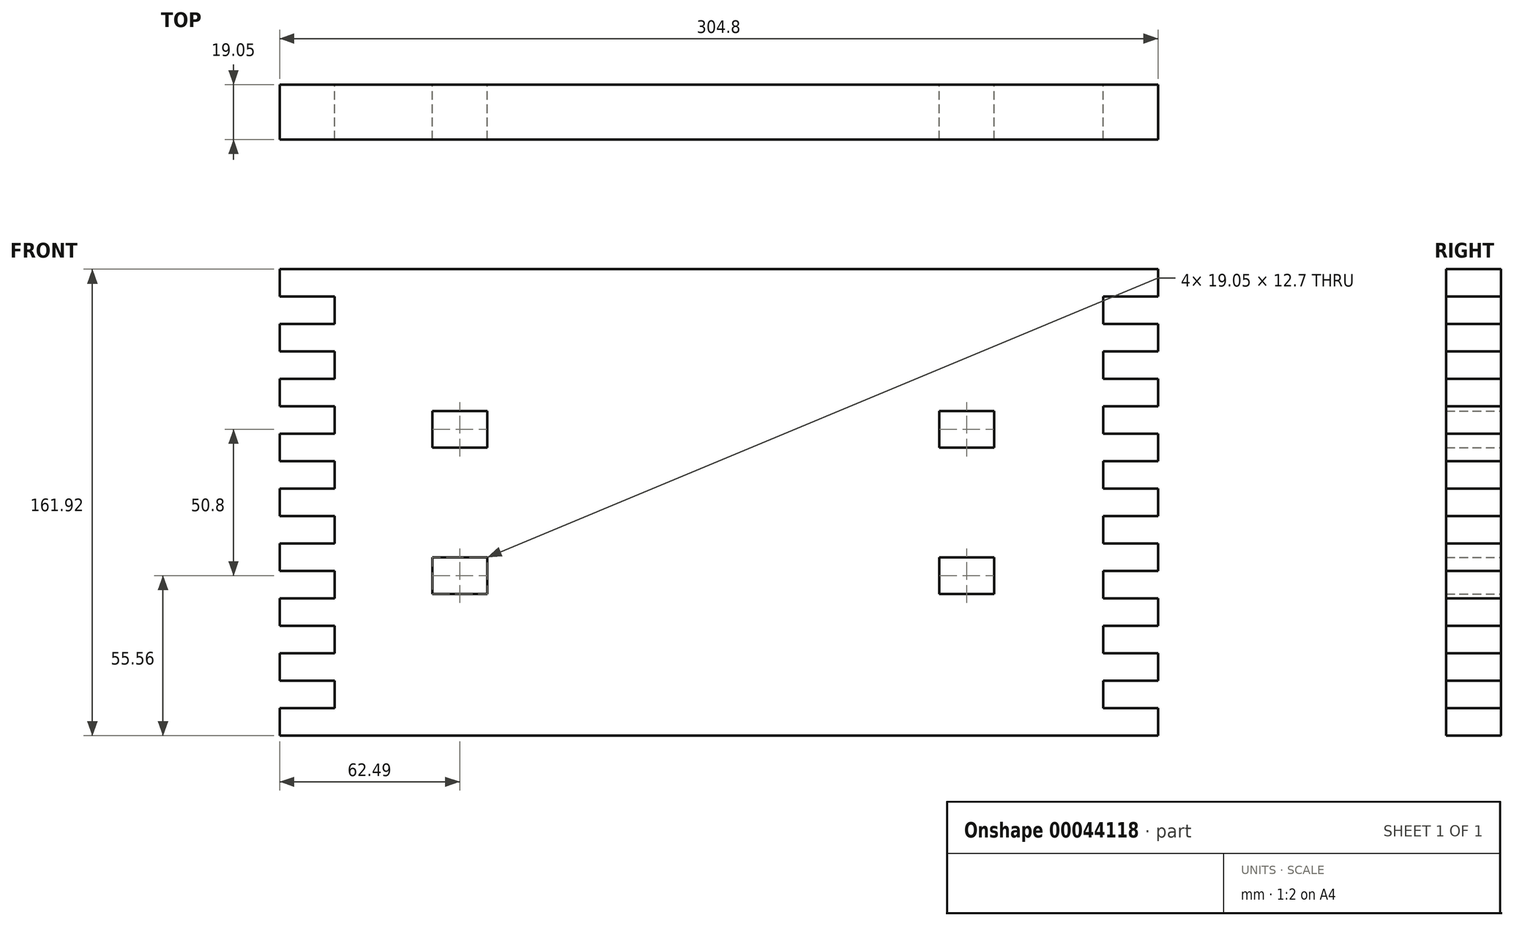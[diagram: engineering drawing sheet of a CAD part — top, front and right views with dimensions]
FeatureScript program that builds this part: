
annotation { "Feature Type Name" : "Feature", "Feature Type Description" : "" }
export const myFeature = defineFeature(function(context is Context, id is Id, definition is map)
    precondition{}
    {
        {
            var Q0;
            Q0=qCreatedBy(makeId("Front.planeOp"),FACE);
            var sketch = newSketch(context, id + "F0", { "sketchPlane" : qUnion([Q0])});
            skPoint(sketch, "E0.rect.middle", {"position": v(0, 0) * mm});
            skLineSegment(sketch, "E1.bottom", {"start": v(-99.44, 19.05) * mm, "end": v(-80.39, 19.05) * mm});
            skLineSegment(sketch, "E1.top", {"start": v(-99.44, 31.75) * mm, "end": v(-80.39, 31.75) * mm});
            skLineSegment(sketch, "E1.left", {"start": v(-99.44, 19.05) * mm, "end": v(-99.44, 31.75) * mm});
            skLineSegment(sketch, "E1.right", {"start": v(-80.39, 19.05) * mm, "end": v(-80.39, 31.75) * mm});
            skLineSegment(sketch, "E2.bottom", {"start": v(-99.44, -19.05) * mm, "end": v(-80.39, -19.05) * mm});
            skLineSegment(sketch, "E2.top", {"start": v(-99.44, -31.75) * mm, "end": v(-80.39, -31.75) * mm});
            skLineSegment(sketch, "E2.left", {"start": v(-99.44, -19.05) * mm, "end": v(-99.44, -31.75) * mm});
            skLineSegment(sketch, "E2.right", {"start": v(-80.39, -19.05) * mm, "end": v(-80.39, -31.75) * mm});
            skLineSegment(sketch, "E3.bottom", {"start": v(76.49, 31.75) * mm, "end": v(95.54, 31.75) * mm});
            skLineSegment(sketch, "E3.top", {"start": v(76.49, 19.05) * mm, "end": v(95.54, 19.05) * mm});
            skLineSegment(sketch, "E3.left", {"start": v(76.49, 31.75) * mm, "end": v(76.49, 19.05) * mm});
            skLineSegment(sketch, "E3.right", {"start": v(95.54, 31.75) * mm, "end": v(95.54, 19.05) * mm});
            skLineSegment(sketch, "E4.bottom", {"start": v(76.49, -19.05) * mm, "end": v(95.54, -19.05) * mm});
            skLineSegment(sketch, "E4.top", {"start": v(76.49, -31.75) * mm, "end": v(95.54, -31.75) * mm});
            skLineSegment(sketch, "E4.left", {"start": v(76.49, -19.05) * mm, "end": v(76.49, -31.75) * mm});
            skLineSegment(sketch, "E4.right", {"start": v(95.54, -19.05) * mm, "end": v(95.54, -31.75) * mm});
            skLineSegment(sketch, "E5", {"start": v(0, -80.96) * mm, "end": v(152.4, -80.96) * mm});
            skLineSegment(sketch, "E6", {"start": v(152.4, 80.96) * mm, "end": v(-152.4, 80.96) * mm});
            skLineSegment(sketch, "E7", {"start": v(133.35, 71.44) * mm, "end": v(133.35, 61.91) * mm});
            skLineSegment(sketch, "E8", {"start": v(133.35, 71.44) * mm, "end": v(152.4, 71.44) * mm});
            skLineSegment(sketch, "E9", {"start": v(152.4, 80.96) * mm, "end": v(152.4, 71.44) * mm});
            skLineSegment(sketch, "E10", {"start": v(133.35, 61.91) * mm, "end": v(152.4, 61.91) * mm});
            skLineSegment(sketch, "E11", {"start": v(152.4, 61.91) * mm, "end": v(152.4, 52.39) * mm});
            skLineSegment(sketch, "E12", {"start": v(152.4, 52.39) * mm, "end": v(133.35, 52.39) * mm});
            skLineSegment(sketch, "E13", {"start": v(133.35, 42.86) * mm, "end": v(152.4, 42.86) * mm});
            skLineSegment(sketch, "E14", {"start": v(152.4, 42.86) * mm, "end": v(152.4, 33.34) * mm});
            skLineSegment(sketch, "E15", {"start": v(152.4, 33.34) * mm, "end": v(133.35, 33.34) * mm});
            skLineSegment(sketch, "E16", {"start": v(133.35, 23.81) * mm, "end": v(152.4, 23.81) * mm});
            skLineSegment(sketch, "E17", {"start": v(152.4, 23.81) * mm, "end": v(152.4, 14.29) * mm});
            skLineSegment(sketch, "E18", {"start": v(152.4, 14.29) * mm, "end": v(133.35, 14.29) * mm});
            skLineSegment(sketch, "E19", {"start": v(133.35, 4.76) * mm, "end": v(152.4, 4.76) * mm});
            skLineSegment(sketch, "E20", {"start": v(152.4, 4.76) * mm, "end": v(152.4, -4.76) * mm});
            skLineSegment(sketch, "E21", {"start": v(152.4, -4.76) * mm, "end": v(133.35, -4.76) * mm});
            skLineSegment(sketch, "E22", {"start": v(133.35, -14.29) * mm, "end": v(152.4, -14.29) * mm});
            skLineSegment(sketch, "E23", {"start": v(152.4, -14.29) * mm, "end": v(152.4, -23.81) * mm});
            skLineSegment(sketch, "E24", {"start": v(152.4, -23.81) * mm, "end": v(133.35, -23.81) * mm});
            skLineSegment(sketch, "E25", {"start": v(133.35, -33.34) * mm, "end": v(152.4, -33.34) * mm});
            skLineSegment(sketch, "E26", {"start": v(152.4, -33.34) * mm, "end": v(152.4, -42.86) * mm});
            skLineSegment(sketch, "E27", {"start": v(152.4, -42.86) * mm, "end": v(133.35, -42.86) * mm});
            skLineSegment(sketch, "E28", {"start": v(133.35, -52.39) * mm, "end": v(152.4, -52.39) * mm});
            skLineSegment(sketch, "E29", {"start": v(152.4, -52.39) * mm, "end": v(152.4, -61.91) * mm});
            skLineSegment(sketch, "E30", {"start": v(152.4, -61.91) * mm, "end": v(133.35, -61.91) * mm});
            skLineSegment(sketch, "E31", {"start": v(152.4, -80.96) * mm, "end": v(152.4, -71.44) * mm});
            skLineSegment(sketch, "E32", {"start": v(152.4, -71.44) * mm, "end": v(133.35, -71.44) * mm});
            skPoint(sketch, "E33.MirrorCS.start.orphan", {"position": v(-152.4, 80.96) * mm});
            skPoint(sketch, "E34.orphan", {"position": v(-152.4, -80.96) * mm});
            skLineSegment(sketch, "E35", {"start": v(0, -80.96) * mm, "end": v(-152.4, -80.96) * mm});
            skLineSegment(sketch, "E36", {"start": v(-152.4, -80.96) * mm, "end": v(-152.4, -71.44) * mm});
            skLineSegment(sketch, "E37", {"start": v(-152.4, -71.44) * mm, "end": v(-133.35, -71.44) * mm});
            skLineSegment(sketch, "E38", {"start": v(-133.35, -71.44) * mm, "end": v(-133.35, -61.91) * mm});
            skLineSegment(sketch, "E39", {"start": v(-133.35, -61.91) * mm, "end": v(-152.4, -61.91) * mm});
            skLineSegment(sketch, "E40", {"start": v(-152.4, -61.91) * mm, "end": v(-152.4, -52.39) * mm});
            skLineSegment(sketch, "E41", {"start": v(-152.4, -52.39) * mm, "end": v(-133.35, -52.39) * mm});
            skLineSegment(sketch, "E42", {"start": v(-133.35, -52.39) * mm, "end": v(-133.35, -42.86) * mm});
            skLineSegment(sketch, "E43", {"start": v(-133.35, -42.86) * mm, "end": v(-152.4, -42.86) * mm});
            skLineSegment(sketch, "E44", {"start": v(-152.4, -42.86) * mm, "end": v(-152.4, -33.34) * mm});
            skLineSegment(sketch, "E45", {"start": v(-152.4, -33.34) * mm, "end": v(-133.35, -33.34) * mm});
            skLineSegment(sketch, "E46", {"start": v(-133.35, -33.34) * mm, "end": v(-133.35, -23.81) * mm});
            skLineSegment(sketch, "E47", {"start": v(-133.35, -23.81) * mm, "end": v(-152.4, -23.81) * mm});
            skLineSegment(sketch, "E48", {"start": v(-152.4, -23.81) * mm, "end": v(-152.4, -14.29) * mm});
            skLineSegment(sketch, "E49", {"start": v(-152.4, -14.29) * mm, "end": v(-133.35, -14.29) * mm});
            skLineSegment(sketch, "E50", {"start": v(-133.35, -14.29) * mm, "end": v(-133.35, -4.76) * mm});
            skLineSegment(sketch, "E51", {"start": v(-133.35, -4.76) * mm, "end": v(-152.4, -4.76) * mm});
            skLineSegment(sketch, "E52", {"start": v(-152.4, -4.76) * mm, "end": v(-152.4, 4.76) * mm});
            skLineSegment(sketch, "E53", {"start": v(-152.4, 4.76) * mm, "end": v(-133.35, 4.76) * mm});
            skLineSegment(sketch, "E54", {"start": v(-133.35, 4.76) * mm, "end": v(-133.35, 14.29) * mm});
            skLineSegment(sketch, "E55", {"start": v(-133.35, 14.29) * mm, "end": v(-152.4, 14.29) * mm});
            skLineSegment(sketch, "E56", {"start": v(-152.4, 14.29) * mm, "end": v(-152.4, 23.81) * mm});
            skLineSegment(sketch, "E57", {"start": v(-152.4, 23.81) * mm, "end": v(-133.35, 23.81) * mm});
            skLineSegment(sketch, "E58", {"start": v(-133.35, 23.81) * mm, "end": v(-133.35, 33.34) * mm});
            skLineSegment(sketch, "E59", {"start": v(-133.35, 33.34) * mm, "end": v(-152.4, 33.34) * mm});
            skLineSegment(sketch, "E60", {"start": v(-152.4, 33.34) * mm, "end": v(-152.4, 42.86) * mm});
            skLineSegment(sketch, "E61", {"start": v(-152.4, 42.86) * mm, "end": v(-133.35, 42.86) * mm});
            skLineSegment(sketch, "E62", {"start": v(-133.35, 42.86) * mm, "end": v(-133.35, 52.39) * mm});
            skLineSegment(sketch, "E63", {"start": v(-133.35, 71.44) * mm, "end": v(-152.4, 71.44) * mm});
            skLineSegment(sketch, "E64", {"start": v(-152.4, 71.44) * mm, "end": v(-152.4, 80.96) * mm});
            skLineSegment(sketch, "E65", {"start": v(-133.35, 52.39) * mm, "end": v(-152.4, 52.39) * mm});
            skLineSegment(sketch, "E66", {"start": v(-152.4, 52.39) * mm, "end": v(-152.4, 61.91) * mm});
            skLineSegment(sketch, "E67", {"start": v(-152.4, 61.91) * mm, "end": v(-133.35, 61.91) * mm});
            skLineSegment(sketch, "E68.trimOffspring", {"start": v(-133.35, 61.91) * mm, "end": v(-133.35, 71.44) * mm});
            skLineSegment(sketch, "E69.trimOffspring", {"start": v(133.35, -61.91) * mm, "end": v(133.35, -71.44) * mm});
            skPoint(sketch, "E70.orphan", {"position": v(133.35, -80.96) * mm});
            skLineSegment(sketch, "E71.trimOffspring", {"start": v(133.35, -42.86) * mm, "end": v(133.35, -52.39) * mm});
            skLineSegment(sketch, "E72.trimOffspring", {"start": v(133.35, -23.81) * mm, "end": v(133.35, -33.34) * mm});
            skLineSegment(sketch, "E73.trimOffspring", {"start": v(133.35, -4.76) * mm, "end": v(133.35, -14.29) * mm});
            skLineSegment(sketch, "E74.trimOffspring", {"start": v(133.35, 14.29) * mm, "end": v(133.35, 4.76) * mm});
            skLineSegment(sketch, "E75.trimOffspring", {"start": v(133.35, 33.34) * mm, "end": v(133.35, 23.81) * mm});
            skPoint(sketch, "E76.orphan", {"position": v(133.35, 80.96) * mm});
            skLineSegment(sketch, "E77.trimOffspring", {"start": v(133.35, 52.39) * mm, "end": v(133.35, 42.86) * mm});
            skSolve(sketch);
        }
        {
            var Q0;
            Q0 = qSketchRegion(id + "F0", true);
            extrude(context, id + "F1", {"entities" : qUnion([Q0]), "depth" : 19.05 * mm});
        }
    });
